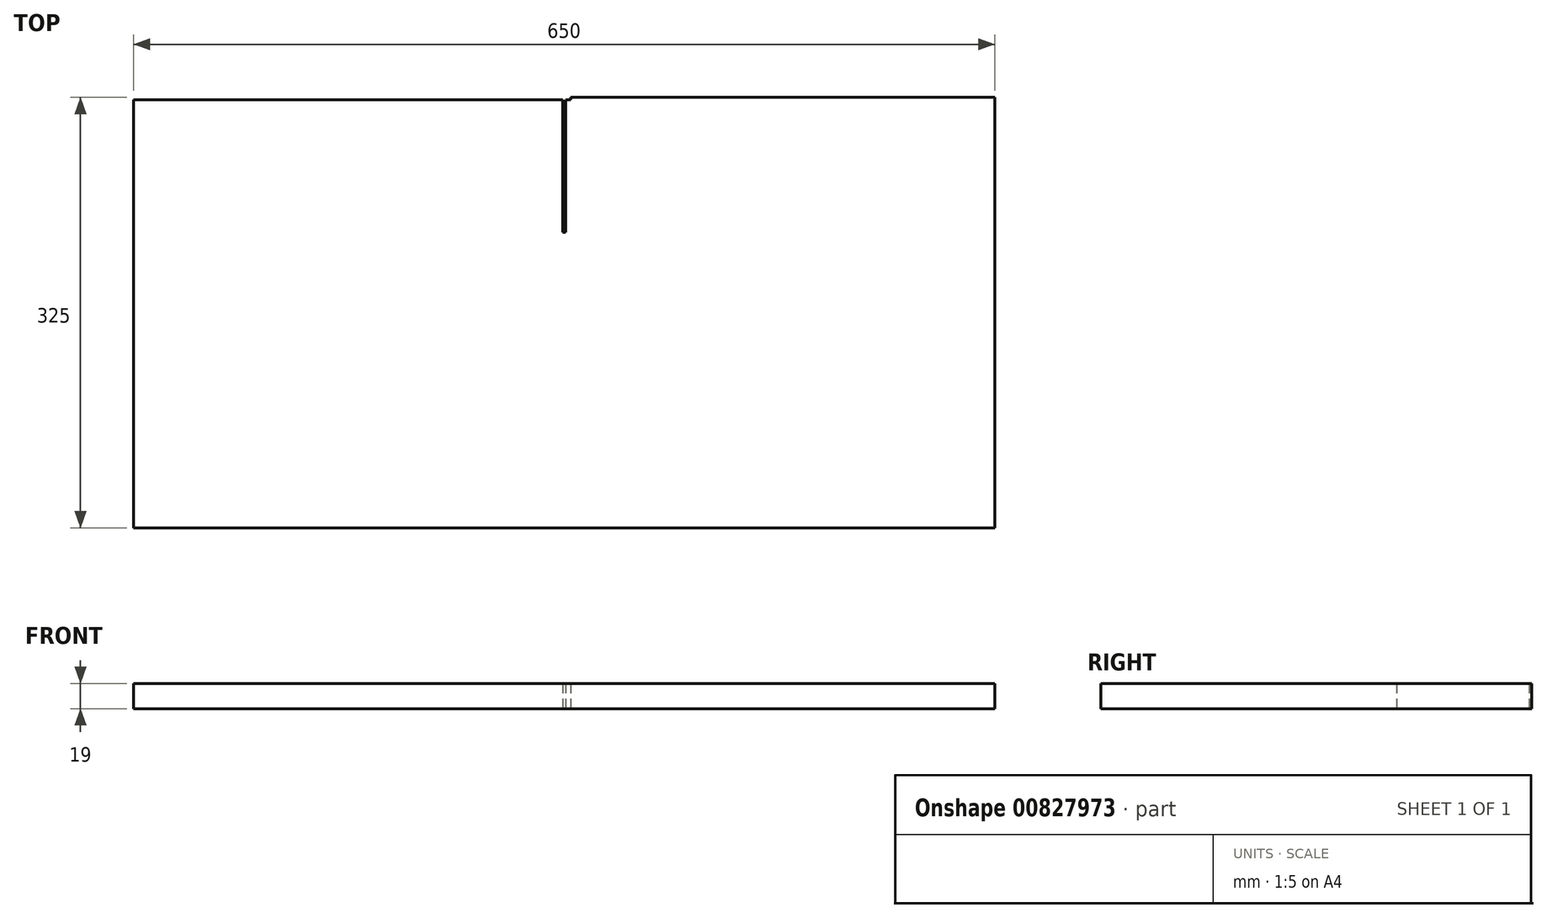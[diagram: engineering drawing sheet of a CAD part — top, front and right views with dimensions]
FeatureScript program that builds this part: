
annotation { "Feature Type Name" : "Feature", "Feature Type Description" : "" }
export const myFeature = defineFeature(function(context is Context, id is Id, definition is map)
    precondition{}
    {
        {
            var Q0;
            Q0=qCreatedBy(makeId("Top.planeOp"),FACE);
            var sketch = newSketch(context, id + "F0", { "sketchPlane" : qUnion([Q0])});
            skLineSegment(sketch, "E0.bottom", {"start": v(-325, 162.5) * mm, "end": v(325, 162.5) * mm});
            skLineSegment(sketch, "E0.top", {"start": v(-325, -162.5) * mm, "end": v(325, -162.5) * mm});
            skLineSegment(sketch, "E0.left", {"start": v(-325, 162.5) * mm, "end": v(-325, -162.5) * mm});
            skLineSegment(sketch, "E0.right", {"start": v(325, 162.5) * mm, "end": v(325, -162.5) * mm});
            skPoint(sketch, "E0.middle", {"position": v(0, 0) * mm});
            skSolve(sketch);
        }
        {
            var Q0;
            Q0=makeQuery(id+"F0.imprint","IMPRINT",FACE,{"disambiguationData":[TD([[makeQuery(id+"F0.imprint","IMPRINT",EDGE,{"derivedFrom":sQuery(id+"F0.wireOp",EDGE,"E0.bottom")}),-1.0]])]});
            extrude(context, id + "F1", {"entities" : qUnion([Q0]), "depth" : 19 * mm, "offsetDistance" : 25 * mm});
        }
        {
            var Q0;
            Q0=makeQuery(id+"F1.opExtrude","SWEPT_FACE",FACE,{"disambiguationData":[OSD([sQuery(id+"F0.wireOp",EDGE,"E0.left")])]});
            var sketch = newSketch(context, id + "F2", { "sketchPlane" : qUnion([Q0])});
            skLineSegment(sketch, "E1.bottom", {"start": v(-162.5, 19) * mm, "end": v(-160.5, 19) * mm});
            skLineSegment(sketch, "E1.top", {"start": v(-162.5, 0) * mm, "end": v(-160.5, 0) * mm});
            skLineSegment(sketch, "E1.left", {"start": v(-162.5, 19) * mm, "end": v(-162.5, 0) * mm});
            skLineSegment(sketch, "E1.right", {"start": v(-160.5, 19) * mm, "end": v(-160.5, 0) * mm});
            skSolve(sketch);
        }
        {
            var Q0;
            Q0 = qSketchRegion(id + "F2", true);
            extrude(context, id + "F3", {"entities" : qUnion([Q0]), "operationType" : NewBodyOperationType.REMOVE, "oppositeDirection" : true, "depth" : 330 * mm, "offsetDistance" : 25 * mm});
        }
        {
            var Q0;
            Q0=makeQuery(id+"F3.boolean.opBoolean","COPY",FACE,{"derivedFrom":makeQuery(id+"F3.opExtrude","SWEPT_FACE",FACE,{"disambiguationData":[OSD([sQuery(id+"F2.wireOp",EDGE,"E1.right")])]})});
            var sketch = newSketch(context, id + "F4", { "sketchPlane" : qUnion([Q0])});
            skLineSegment(sketch, "E2.bottom", {"start": v(-1, 19) * mm, "end": v(1, 19) * mm});
            skLineSegment(sketch, "E2.top", {"start": v(-1, 0) * mm, "end": v(1, 0) * mm});
            skLineSegment(sketch, "E2.left", {"start": v(-1, 19) * mm, "end": v(-1, 0) * mm});
            skLineSegment(sketch, "E2.right", {"start": v(1, 19) * mm, "end": v(1, 0) * mm});
            skPoint(sketch, "E3", {"position": v(0, 0) * mm});
            skSolve(sketch);
        }
        {
            var Q0;
            Q0 = qSketchRegion(id + "F4", true);
            extrude(context, id + "F5", {"entities" : qUnion([Q0]), "operationType" : NewBodyOperationType.REMOVE, "oppositeDirection" : true, "depth" : 100 * mm, "offsetDistance" : 25 * mm});
        }
    });
